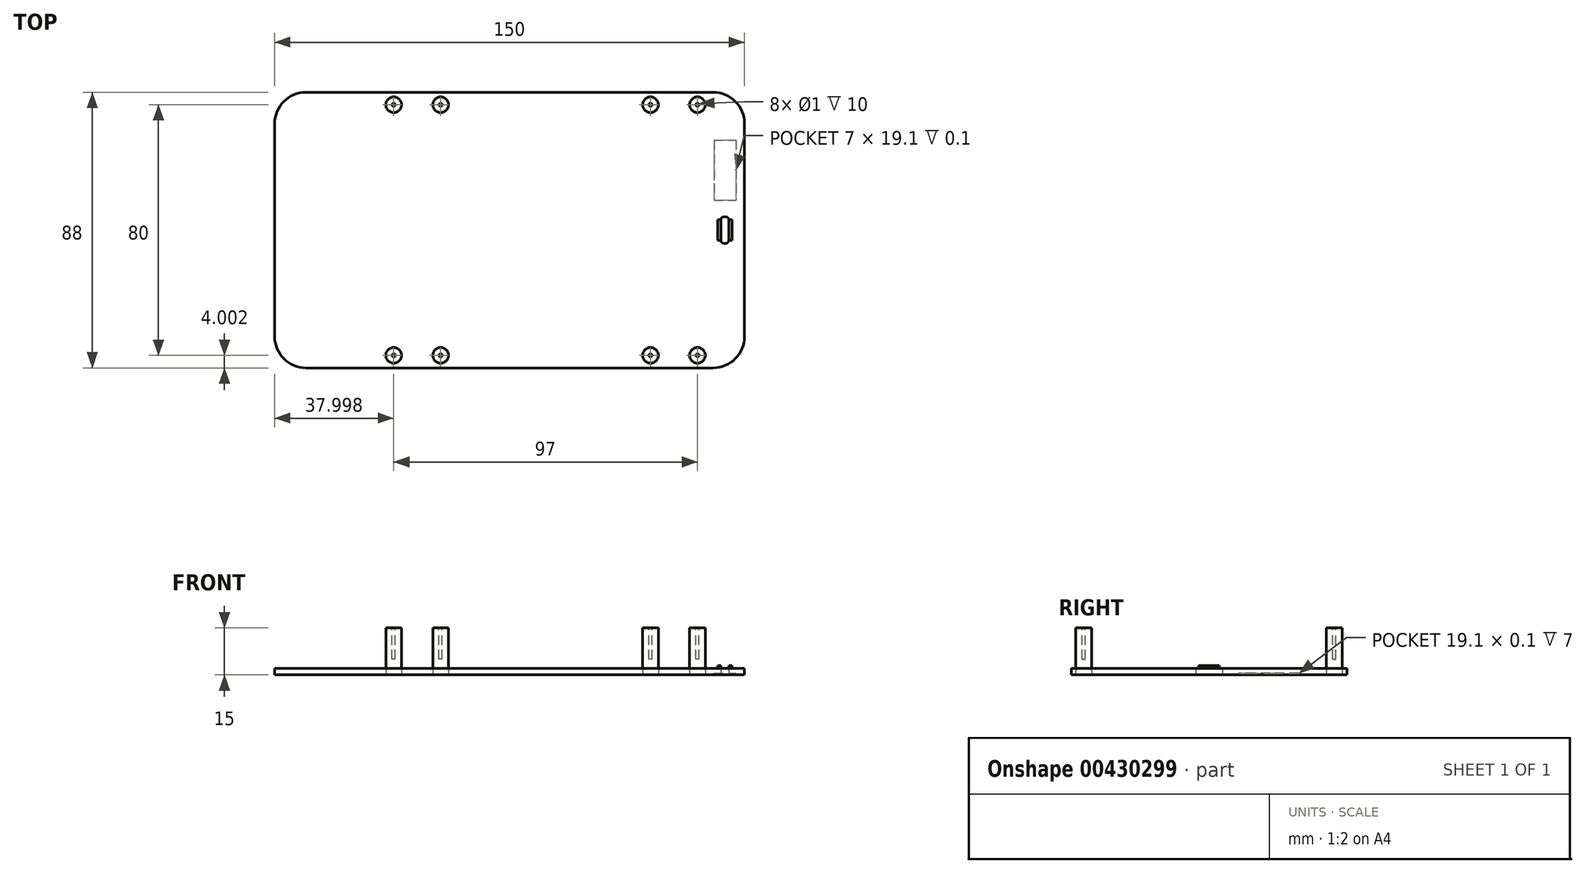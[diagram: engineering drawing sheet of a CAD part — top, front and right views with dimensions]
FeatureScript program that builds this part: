
annotation { "Feature Type Name" : "Feature", "Feature Type Description" : "" }
export const myFeature = defineFeature(function(context is Context, id is Id, definition is map)
    precondition{}
    {
        {
            var Q0;
            Q0=qCreatedBy(makeId("Top.planeOp"),FACE);
            var sketch = newSketch(context, id + "F0", { "sketchPlane" : qUnion([Q0])});
            skLineSegment(sketch, "E0.bottom", {"start": v(-95.35, 34.5) * mm, "end": v(54.65, 34.5) * mm});
            skLineSegment(sketch, "E0.top", {"start": v(-95.35, -53.5) * mm, "end": v(54.65, -53.5) * mm});
            skLineSegment(sketch, "E0.left", {"start": v(-95.35, 34.5) * mm, "end": v(-95.35, -53.5) * mm});
            skLineSegment(sketch, "E0.right", {"start": v(54.65, 34.5) * mm, "end": v(54.65, -53.5) * mm});
            skSolve(sketch);
        }
        {
            var Q0;
            Q0=makeQuery(id+"F0.imprint","IMPRINT",FACE,{"disambiguationData":[TD([[makeQuery(id+"F0.imprint","IMPRINT",EDGE,{"derivedFrom":sQuery(id+"F0.wireOp",EDGE,"E0.bottom")}),-1.0]])]});
            extrude(context, id + "F1", {"entities" : qUnion([Q0]), "depth" : 2 * mm});
        }
        {
            var Q0;
            Q0=qCreatedBy(makeId("Top.planeOp"),FACE);
            var sketch = newSketch(context, id + "F2", { "sketchPlane" : qUnion([Q0])});
            skCircle(sketch, "E1", {"center": v(39.65, -49.5) * mm, "radius": 2.5 * mm});
            skSolve(sketch);
        }
        {
            var Q0;
            Q0 = qSketchRegion(id + "F2", true);
            extrude(context, id + "F3", {"entities" : qUnion([Q0]), "depth" : 15 * mm});
        }
        {
            var Q0;
            Q0=makeQuery(id+"F3.opExtrude","CAP_FACE",FACE,{"disambiguationData":[OSD([sQuery(id+"F2.wireOp",EDGE,"E1")])],"isStart":false});
            var sketch = newSketch(context, id + "F4", { "sketchPlane" : qUnion([Q0])});
            skCircle(sketch, "E2", {"center": v(39.65, -49.5) * mm, "radius": 0.5 * mm});
            skSolve(sketch);
        }
        {
            var Q0;
            Q0 = qSketchRegion(id + "F4", true);
            extrude(context, id + "F5", {"entities" : qUnion([Q0]), "operationType" : NewBodyOperationType.REMOVE, "oppositeDirection" : true, "depth" : 10 * mm});
        }
        {
            var Q0;
            Q0=makeQuery(id+"F3.opExtrude","SWEPT_BODY",BODY,{"disambiguationData":[OSD([sQuery(id+"F2.wireOp",EDGE,"E1")])]});
            transform(context, id + "F6", {"entities" : qUnion([Q0]), "transformType" : TransformType.TRANSLATION_3D, "dx" : -15 * mm, "dy" : 0 * mm, "dz" : 0 * mm, "makeCopy" : true});
        }
        {
            var Q0;
            Q0=makeQuery(id+"F6.opPattern","COPY",BODY,{"derivedFrom":makeQuery(id+"F3.opExtrude","SWEPT_BODY",BODY,{"disambiguationData":[OSD([sQuery(id+"F2.wireOp",EDGE,"E1")])]}),"instanceName":"1"});
            transform(context, id + "F7", {"entities" : qUnion([Q0]), "transformType" : TransformType.TRANSLATION_3D, "dx" : -67 * mm, "dy" : 0 * mm, "dz" : 0 * mm, "makeCopy" : true});
        }
        {
            var Q0;
            Q0=makeQuery(id+"F7.opPattern","COPY",BODY,{"derivedFrom":makeQuery(id+"F6.opPattern","COPY",BODY,{"derivedFrom":makeQuery(id+"F3.opExtrude","SWEPT_BODY",BODY,{"disambiguationData":[OSD([sQuery(id+"F2.wireOp",EDGE,"E1")])]}),"instanceName":"1"}),"instanceName":"1"});
            transform(context, id + "F8", {"entities" : qUnion([Q0]), "transformType" : TransformType.TRANSLATION_3D, "dx" : -15 * mm, "dy" : 0 * mm, "dz" : 0 * mm, "makeCopy" : true});
        }
        {
            var Q0;
            Q0=makeQuery(id+"F8.opPattern","COPY",BODY,{"derivedFrom":makeQuery(id+"F7.opPattern","COPY",BODY,{"derivedFrom":makeQuery(id+"F6.opPattern","COPY",BODY,{"derivedFrom":makeQuery(id+"F3.opExtrude","SWEPT_BODY",BODY,{"disambiguationData":[OSD([sQuery(id+"F2.wireOp",EDGE,"E1")])]}),"instanceName":"1"}),"instanceName":"1"}),"instanceName":"1"});
            transform(context, id + "F9", {"entities" : qUnion([Q0]), "transformType" : TransformType.TRANSLATION_3D, "dx" : 0 * mm, "dy" : 80 * mm, "dz" : 0 * mm, "makeCopy" : true});
        }
        {
            var Q0;
            Q0=makeQuery(id+"F9.opPattern","COPY",BODY,{"derivedFrom":makeQuery(id+"F8.opPattern","COPY",BODY,{"derivedFrom":makeQuery(id+"F7.opPattern","COPY",BODY,{"derivedFrom":makeQuery(id+"F6.opPattern","COPY",BODY,{"derivedFrom":makeQuery(id+"F3.opExtrude","SWEPT_BODY",BODY,{"disambiguationData":[OSD([sQuery(id+"F2.wireOp",EDGE,"E1")])]}),"instanceName":"1"}),"instanceName":"1"}),"instanceName":"1"}),"instanceName":"1"});
            transform(context, id + "F10", {"entities" : qUnion([Q0]), "transformType" : TransformType.TRANSLATION_3D, "dx" : 15 * mm, "dy" : 0 * mm, "dz" : 0 * mm, "makeCopy" : true});
        }
        {
            var Q0;
            Q0=makeQuery(id+"F10.opPattern","COPY",BODY,{"derivedFrom":makeQuery(id+"F9.opPattern","COPY",BODY,{"derivedFrom":makeQuery(id+"F8.opPattern","COPY",BODY,{"derivedFrom":makeQuery(id+"F7.opPattern","COPY",BODY,{"derivedFrom":makeQuery(id+"F6.opPattern","COPY",BODY,{"derivedFrom":makeQuery(id+"F3.opExtrude","SWEPT_BODY",BODY,{"disambiguationData":[OSD([sQuery(id+"F2.wireOp",EDGE,"E1")])]}),"instanceName":"1"}),"instanceName":"1"}),"instanceName":"1"}),"instanceName":"1"}),"instanceName":"1"});
            transform(context, id + "F11", {"entities" : qUnion([Q0]), "transformType" : TransformType.TRANSLATION_3D, "dx" : 67 * mm, "dy" : 0 * mm, "dz" : 0 * mm, "makeCopy" : true});
        }
        {
            var Q0;
            Q0=makeQuery(id+"F11.opPattern","COPY",BODY,{"derivedFrom":makeQuery(id+"F10.opPattern","COPY",BODY,{"derivedFrom":makeQuery(id+"F9.opPattern","COPY",BODY,{"derivedFrom":makeQuery(id+"F8.opPattern","COPY",BODY,{"derivedFrom":makeQuery(id+"F7.opPattern","COPY",BODY,{"derivedFrom":makeQuery(id+"F6.opPattern","COPY",BODY,{"derivedFrom":makeQuery(id+"F3.opExtrude","SWEPT_BODY",BODY,{"disambiguationData":[OSD([sQuery(id+"F2.wireOp",EDGE,"E1")])]}),"instanceName":"1"}),"instanceName":"1"}),"instanceName":"1"}),"instanceName":"1"}),"instanceName":"1"}),"instanceName":"1"});
            transform(context, id + "F12", {"entities" : qUnion([Q0]), "transformType" : TransformType.TRANSLATION_3D, "dx" : 15 * mm, "dy" : 0 * mm, "dz" : 0 * mm, "makeCopy" : true});
        }
        {
            var Q0;
            Q0=makeQuery(id+"F1.opExtrude","SWEPT_EDGE",EDGE,{"disambiguationData":[OSD([sQuery(id+"F0.wireOp",EDGE,"E0.top"),sQuery(id+"F0.wireOp",EDGE,"E0.left")])]});
            var Q1;
            Q1=makeQuery(id+"F1.opExtrude","SWEPT_EDGE",EDGE,{"disambiguationData":[OSD([sQuery(id+"F0.wireOp",EDGE,"E0.top"),sQuery(id+"F0.wireOp",EDGE,"E0.right")])]});
            var Q2;
            Q2=makeQuery(id+"F1.opExtrude","SWEPT_EDGE",EDGE,{"disambiguationData":[OSD([sQuery(id+"F0.wireOp",EDGE,"E0.bottom"),sQuery(id+"F0.wireOp",EDGE,"E0.right")])]});
            var Q3;
            Q3=makeQuery(id+"F1.opExtrude","SWEPT_EDGE",EDGE,{"disambiguationData":[OSD([sQuery(id+"F0.wireOp",EDGE,"E0.bottom"),sQuery(id+"F0.wireOp",EDGE,"E0.left")])]});
            fillet(context, id + "F13", {"entities" : qUnion([Q0, Q1, Q2, Q3]), "radius" : 10 * mm, "tangentPropagation" : true, "allowEdgeOverflow" : false});
        }
        {
            var Q0;
            Q0=qCreatedBy(makeId("Top.planeOp"),FACE);
            var sketch = newSketch(context, id + "F14", { "sketchPlane" : qUnion([Q0])});
            skLineSegment(sketch, "E3.bottom", {"start": v(47.15, -5.25) * mm, "end": v(49.65, -5.25) * mm});
            skLineSegment(sketch, "E3.top", {"start": v(47.15, -13.75) * mm, "end": v(49.65, -13.75) * mm});
            skLineSegment(sketch, "E3.left", {"start": v(47.15, -5.25) * mm, "end": v(47.15, -13.75) * mm});
            skLineSegment(sketch, "E3.right", {"start": v(49.65, -5.25) * mm, "end": v(49.65, -13.75) * mm});
            skSolve(sketch);
        }
        {
            var Q0;
            Q0 = qSketchRegion(id + "F14", true);
            extrude(context, id + "F15", {"entities" : qUnion([Q0]), "operationType" : NewBodyOperationType.REMOVE, "depth" : 4 * mm});
        }
        {
            var Q0;
            Q0=makeQuery(id+"F15.boolean.opBoolean","COPY",EDGE,{"derivedFrom":makeQuery(id+"F15.opExtrude","SWEPT_EDGE",EDGE,{"disambiguationData":[OSD([sQuery(id+"F14.wireOp",EDGE,"E3.bottom"),sQuery(id+"F14.wireOp",EDGE,"E3.right")])]})});
            var Q1;
            Q1=makeQuery(id+"F15.boolean.opBoolean","COPY",EDGE,{"derivedFrom":makeQuery(id+"F15.opExtrude","SWEPT_EDGE",EDGE,{"disambiguationData":[OSD([sQuery(id+"F14.wireOp",EDGE,"E3.bottom"),sQuery(id+"F14.wireOp",EDGE,"E3.left")])]})});
            var Q2;
            Q2=makeQuery(id+"F15.boolean.opBoolean","COPY",EDGE,{"derivedFrom":makeQuery(id+"F15.opExtrude","SWEPT_EDGE",EDGE,{"disambiguationData":[OSD([sQuery(id+"F14.wireOp",EDGE,"E3.top"),sQuery(id+"F14.wireOp",EDGE,"E3.left")])]})});
            var Q3;
            Q3=makeQuery(id+"F15.boolean.opBoolean","COPY",EDGE,{"derivedFrom":makeQuery(id+"F15.opExtrude","SWEPT_EDGE",EDGE,{"disambiguationData":[OSD([sQuery(id+"F14.wireOp",EDGE,"E3.top"),sQuery(id+"F14.wireOp",EDGE,"E3.right")])]})});
            fillet(context, id + "F16", {"entities" : qUnion([Q0, Q1, Q2, Q3]), "radius" : 1 * mm, "tangentPropagation" : true, "allowEdgeOverflow" : false});
        }
        {
            var Q0;
            Q0=makeQuery(id+"F1.opExtrude","CAP_FACE",FACE,{"disambiguationData":[OSD([sQuery(id+"F0.wireOp",EDGE,"E0.bottom"),sQuery(id+"F0.wireOp",EDGE,"E0.top"),sQuery(id+"F0.wireOp",EDGE,"E0.left"),sQuery(id+"F0.wireOp",EDGE,"E0.right")])],"isStart":false});
            var sketch = newSketch(context, id + "F17", { "sketchPlane" : qUnion([Q0])});
            skLineSegment(sketch, "E4.bottom", {"start": v(47.15, -6.25) * mm, "end": v(46.15, -6.25) * mm});
            skLineSegment(sketch, "E4.top", {"start": v(47.15, -12.75) * mm, "end": v(46.15, -12.75) * mm});
            skLineSegment(sketch, "E4.left", {"start": v(47.15, -6.25) * mm, "end": v(47.15, -12.75) * mm});
            skLineSegment(sketch, "E4.right", {"start": v(46.15, -6.25) * mm, "end": v(46.15, -12.75) * mm});
            skSolve(sketch);
        }
        {
            var Q0;
            Q0 = qSketchRegion(id + "F17", true);
            extrude(context, id + "F18", {"entities" : qUnion([Q0]), "depth" : 1 * mm});
        }
        {
            var Q0;
            Q0=makeQuery(id+"F18.opExtrude","SWEPT_BODY",BODY,{"disambiguationData":[OSD([sQuery(id+"F17.wireOp",EDGE,"E4.bottom"),sQuery(id+"F17.wireOp",EDGE,"E4.top"),sQuery(id+"F17.wireOp",EDGE,"E4.left"),sQuery(id+"F17.wireOp",EDGE,"E4.right")])]});
            transform(context, id + "F19", {"entities" : qUnion([Q0]), "transformType" : TransformType.TRANSLATION_3D, "dx" : 3.5 * mm, "dy" : 0 * mm, "dz" : 0 * mm, "makeCopy" : true});
        }
        {
            var Q0;
            Q0=qCreatedBy(makeId("Top.planeOp"),FACE);
            cPlane(context, id + "F20", {"entities" : qUnion([Q0]), "cplaneType" : CPlaneType.OFFSET, "offset" : 0.5 * mm, "width" : 150 * mm, "height" : 150 * mm});
        }
        {
            var Q0;
            Q0=qCreatedBy(id+"F20.planeOp",FACE);
            var sketch = newSketch(context, id + "F21", { "sketchPlane" : qUnion([Q0])});
            skLineSegment(sketch, "E5.bottom", {"start": v(44.95, 19.15) * mm, "end": v(51.95, 19.15) * mm});
            skLineSegment(sketch, "E5.top", {"start": v(44.95, 0.05) * mm, "end": v(51.95, 0.05) * mm});
            skLineSegment(sketch, "E5.left", {"start": v(44.95, 19.15) * mm, "end": v(44.95, 0.05) * mm});
            skLineSegment(sketch, "E5.right", {"start": v(51.95, 19.15) * mm, "end": v(51.95, 0.05) * mm});
            skSolve(sketch);
        }
        {
            var Q0;
            Q0 = qSketchRegion(id + "F21", true);
            extrude(context, id + "F22", {"entities" : qUnion([Q0]), "operationType" : NewBodyOperationType.REMOVE, "oppositeDirection" : true, "depth" : 0.1 * mm});
        }
    });
